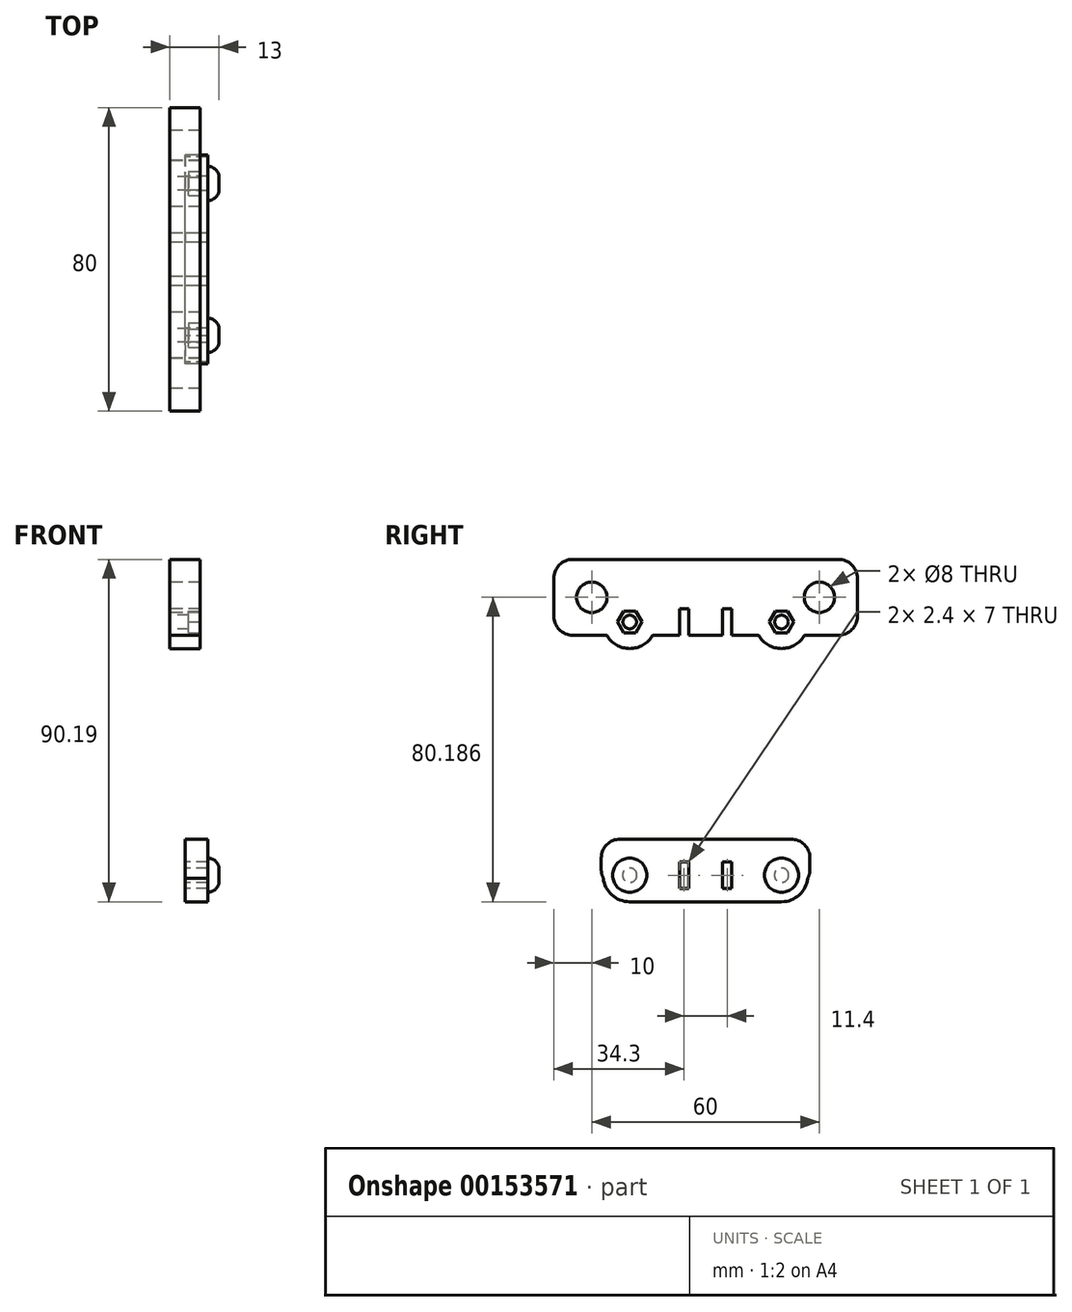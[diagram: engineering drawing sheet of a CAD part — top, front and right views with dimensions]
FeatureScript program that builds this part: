
annotation { "Feature Type Name" : "Feature", "Feature Type Description" : "" }
export const myFeature = defineFeature(function(context is Context, id is Id, definition is map)
    precondition{}
    {
        {
            var Q0;
            Q0=qCreatedBy(makeId("Right.planeOp"),FACE);
            var sketch = newSketch(context, id + "F0", { "sketchPlane" : qUnion([Q0])});
            skLineSegment(sketch, "E0", {"start": v(0, 142.5) * mm, "end": v(0, -139.74) * mm, "construction": true});
            skLineSegment(sketch, "E1.bottom", {"start": v(-35, 25) * mm, "end": v(35, 25) * mm});
            skLineSegment(sketch, "E1.top", {"start": v(-40, -25) * mm, "end": v(40, -25) * mm});
            skLineSegment(sketch, "E1.left", {"start": v(-40, 20) * mm, "end": v(-40, -25) * mm});
            skLineSegment(sketch, "E1.right", {"start": v(40, 20) * mm, "end": v(40, -25) * mm});
            skPoint(sketch, "E1.middle", {"position": v(0, 0) * mm});
            skCircle(sketch, "E2", {"center": v(-30, 13) * mm, "radius": 4 * mm});
            skCircle(sketch, "E3", {"center": v(30, 13) * mm, "radius": 4 * mm});
            skCircle(sketch, "E4", {"center": v(-30, -13) * mm, "radius": 5 * mm});
            skCircle(sketch, "E5", {"center": v(30, -13) * mm, "radius": 5 * mm});
            skPoint(sketch, "E6.visualSharp", {"position": v(-40, 25) * mm});
            skArc(sketch, "E6.filletArc", {"start": v(-35, 25) * mm, "mid": v(-38.54, 23.54) * mm, "end": v(-40, 20) * mm});
            skPoint(sketch, "E7.visualSharp", {"position": v(40, 25) * mm});
            skArc(sketch, "E7.filletArc", {"start": v(40, 20) * mm, "mid": v(38.54, 23.54) * mm, "end": v(35, 25) * mm});
            skLineSegment(sketch, "E8.bottom", {"start": v(-11, 25) * mm, "end": v(11, 25) * mm});
            skLineSegment(sketch, "E8.top", {"start": v(-9, 8) * mm, "end": v(9, 8) * mm});
            skLineSegment(sketch, "E8.left", {"start": v(-11, 25) * mm, "end": v(-11, 10) * mm});
            skLineSegment(sketch, "E8.right", {"start": v(11, 25) * mm, "end": v(11, 10) * mm});
            skPoint(sketch, "E8.middle", {"position": v(0, 16.5) * mm});
            skPoint(sketch, "E9.visualSharp", {"position": v(11, 8) * mm});
            skArc(sketch, "E9.filletArc", {"start": v(9, 8) * mm, "mid": v(10.41, 8.59) * mm, "end": v(11, 10) * mm});
            skPoint(sketch, "E10.visualSharp", {"position": v(-11, 8) * mm});
            skArc(sketch, "E10.filletArc", {"start": v(-11, 10) * mm, "mid": v(-10.41, 8.59) * mm, "end": v(-9, 8) * mm});
            skSolve(sketch);
        }
        {
            var Q0;
            Q0=makeQuery(id+"F0.imprint","IMPRINT",FACE,{"disambiguationData":[TD([[makeQuery(id+"F0.imprint","IMPRINT",EDGE,{"derivedFrom":sQuery(id+"F0.wireOp",EDGE,"E1.bottom")}),-1.0]])]});
            extrude(context, id + "F1", {"entities" : qUnion([Q0]), "depth" : 8 * mm, "symmetric" : true});
        }
        {
            var Q0;
            {var subQ0=sQuery(id+"F0.wireOp",EDGE,"E1.bottom");Q0=makeQuery(id+"F1.opExtrude","SWEPT_FACE",FACE,{"disambiguationData":[OSD([subQ0]),TDD([makeQuery(id+"F0.imprint","IMPRINT",EDGE,{"disambiguationData":[TD([[makeQuery(id+"F0.imprint","INTERSECT",VERTEX,{"derivedFrom":[subQ0,sQuery(id+"F0.wireOp",EDGE,"E7.filletArc")]}),1.0]])],"derivedFrom":subQ0})])]});}
            var sketch = newSketch(context, id + "F2", { "sketchPlane" : qUnion([Q0])});
            skCircle(sketch, "E11", {"center": v(0, 30) * mm, "radius": 1.4 * mm});
            skCircle(sketch, "E12", {"center": v(0, 24) * mm, "radius": 1.4 * mm});
            skCircle(sketch, "E13", {"center": v(0, -24) * mm, "radius": 1.4 * mm});
            skCircle(sketch, "E14", {"center": v(0, -30) * mm, "radius": 1.4 * mm});
            skLineSegment(sketch, "E15", {"start": v(-76.86, 0) * mm, "end": v(82.98, 0) * mm, "construction": true});
            skSolve(sketch);
        }
        {
            var Q0;
            Q0=qSketchRegion(id+"F2",true);
            extrude(context, id + "F3", {"entities" : qUnion([Q0]), "operationType" : NewBodyOperationType.REMOVE, "oppositeDirection" : true, "depth" : 13 * mm});
        }
        {
            var Q0;
            Q0=qCreatedBy(makeId("Right.planeOp"),FACE);
            var sketch = newSketch(context, id + "F4", { "sketchPlane" : qUnion([Q0])});
            skLineSegment(sketch, "E16", {"start": v(0, 90) * mm, "end": v(0, 27.03) * mm, "construction": true});
            skCircle(sketch, "E17", {"center": v(-30, 70.19) * mm, "radius": 4 * mm});
            skCircle(sketch, "E18", {"center": v(30, 70.19) * mm, "radius": 4 * mm});
            skLineSegment(sketch, "E19.bottom", {"start": v(-35, 80.19) * mm, "end": v(35, 80.19) * mm});
            skLineSegment(sketch, "E19.top", {"start": v(-35, 60.19) * mm, "end": v(-26.06, 60.19) * mm});
            skLineSegment(sketch, "E19.left", {"start": v(-40, 75.19) * mm, "end": v(-40, 65.19) * mm});
            skLineSegment(sketch, "E19.right", {"start": v(40, 75.19) * mm, "end": v(40, 65.19) * mm});
            skPoint(sketch, "E19.middle", {"position": v(0, 70.19) * mm});
            skPoint(sketch, "E20.visualSharp", {"position": v(-40, 80.19) * mm});
            skArc(sketch, "E20.filletArc", {"start": v(-35, 80.19) * mm, "mid": v(-38.54, 78.72) * mm, "end": v(-40, 75.19) * mm});
            skPoint(sketch, "E21.visualSharp", {"position": v(-40, 60.19) * mm});
            skArc(sketch, "E21.filletArc", {"start": v(-40, 65.19) * mm, "mid": v(-38.54, 61.65) * mm, "end": v(-35, 60.19) * mm});
            skPoint(sketch, "E22.visualSharp", {"position": v(40, 80.19) * mm});
            skArc(sketch, "E22.filletArc", {"start": v(40, 75.19) * mm, "mid": v(38.54, 78.72) * mm, "end": v(35, 80.19) * mm});
            skPoint(sketch, "E23.visualSharp", {"position": v(40, 60.19) * mm});
            skArc(sketch, "E23.filletArc", {"start": v(35, 60.19) * mm, "mid": v(38.54, 61.65) * mm, "end": v(40, 65.19) * mm});
            skLineSegment(sketch, "E24.bottom", {"start": v(-11, 80.19) * mm, "end": v(11, 80.19) * mm});
            skPoint(sketch, "E24.middle", {"position": v(0, 76.69) * mm});
            skLineSegment(sketch, "E25", {"start": v(-87.97, 70.19) * mm, "end": v(-87.97, 70.19) * mm});
            skPoint(sketch, "E25.endSnap0", {"position": v(40, 70.19) * mm});
            skLineSegment(sketch, "E26.bottom", {"start": v(-6.9, 67.19) * mm, "end": v(-4.5, 67.19) * mm});
            skLineSegment(sketch, "E26.top", {"start": v(-6.9, 60.19) * mm, "end": v(-4.5, 60.19) * mm});
            skLineSegment(sketch, "E26.left", {"start": v(-6.9, 67.19) * mm, "end": v(-6.9, 60.19) * mm});
            skLineSegment(sketch, "E26.right", {"start": v(-4.5, 67.19) * mm, "end": v(-4.5, 60.19) * mm});
            skLineSegment(sketch, "E27.bottom", {"start": v(4.5, 67.19) * mm, "end": v(6.9, 67.19) * mm});
            skLineSegment(sketch, "E27.top", {"start": v(4.5, 60.19) * mm, "end": v(6.9, 60.19) * mm});
            skLineSegment(sketch, "E27.left", {"start": v(4.5, 67.19) * mm, "end": v(4.5, 60.19) * mm});
            skLineSegment(sketch, "E27.right", {"start": v(6.9, 67.19) * mm, "end": v(6.9, 60.19) * mm});
            skCircle(sketch, "E28", {"center": v(-20, 63.69) * mm, "radius": 1.8 * mm});
            skCircle(sketch, "E29", {"center": v(20, 63.69) * mm, "radius": 1.8 * mm});
            skArc(sketch, "E30", {"start": v(-26.06, 60.19) * mm, "mid": v(-20, 56.69) * mm, "end": v(-13.94, 60.19) * mm});
            skArc(sketch, "E31.MirrorC", {"start": v(26.06, 60.19) * mm, "mid": v(20, 56.69) * mm, "end": v(13.94, 60.19) * mm});
            skLineSegment(sketch, "E32.trimOffspring", {"start": v(-13.94, 60.19) * mm, "end": v(13.94, 60.19) * mm});
            skLineSegment(sketch, "E33.trimOffspring", {"start": v(26.06, 60.19) * mm, "end": v(35, 60.19) * mm});
            skSolve(sketch);
        }
        {
            var Q0;
            Q0=makeQuery(id+"F4.imprint","IMPRINT",FACE,{"disambiguationData":[TD([[makeQuery(id+"F4.imprint","IMPRINT",EDGE,{"derivedFrom":sQuery(id+"F4.wireOp",EDGE,"E17")}),-1.0]])]});
            extrude(context, id + "F5", {"entities" : qUnion([Q0]), "depth" : 8 * mm, "symmetric" : true});
        }
        {
            var Q0;
            Q0=makeQuery(id+"F5.opExtrude","CAP_FACE",FACE,{"disambiguationData":[OSD([sQuery(id+"F4.wireOp",EDGE,"E17"),sQuery(id+"F4.wireOp",EDGE,"E18"),sQuery(id+"F4.wireOp",EDGE,"E19.bottom"),sQuery(id+"F4.wireOp",EDGE,"E19.top"),sQuery(id+"F4.wireOp",EDGE,"E19.left"),sQuery(id+"F4.wireOp",EDGE,"E19.right"),sQuery(id+"F4.wireOp",EDGE,"E20.filletArc"),sQuery(id+"F4.wireOp",EDGE,"E21.filletArc"),sQuery(id+"F4.wireOp",EDGE,"E22.filletArc"),sQuery(id+"F4.wireOp",EDGE,"E23.filletArc"),sQuery(id+"F4.wireOp",EDGE,"E24.bottom"),sQuery(id+"F4.wireOp",EDGE,"E26.bottom"),sQuery(id+"F4.wireOp",EDGE,"E26.left"),sQuery(id+"F4.wireOp",EDGE,"E26.right"),sQuery(id+"F4.wireOp",EDGE,"E27.bottom"),sQuery(id+"F4.wireOp",EDGE,"E27.left"),sQuery(id+"F4.wireOp",EDGE,"E27.right"),sQuery(id+"F4.wireOp",EDGE,"E28"),sQuery(id+"F4.wireOp",EDGE,"E29")])],"isStart":false});
            var sketch = newSketch(context, id + "F6", { "sketchPlane" : qUnion([Q0])});
            skCircle(sketch, "E34.cCircle", {"center": v(20, 63.69) * mm, "radius": 2.8 * mm, "construction": true});
            skLineSegment(sketch, "E34.0", {"start": v(18.38, 66.49) * mm, "end": v(21.62, 66.49) * mm});
            skLineSegment(sketch, "E34.1", {"start": v(21.62, 66.49) * mm, "end": v(23.23, 63.69) * mm});
            skLineSegment(sketch, "E34.2", {"start": v(23.23, 63.69) * mm, "end": v(21.62, 60.89) * mm});
            skLineSegment(sketch, "E34.3", {"start": v(21.62, 60.89) * mm, "end": v(18.38, 60.89) * mm});
            skLineSegment(sketch, "E34.4", {"start": v(18.38, 60.89) * mm, "end": v(16.77, 63.69) * mm});
            skLineSegment(sketch, "E34.5", {"start": v(16.77, 63.69) * mm, "end": v(18.38, 66.49) * mm});
            skPoint(sketch, "E34.0.midPoint", {"position": v(20, 66.49) * mm});
            skCircle(sketch, "E35.cCircle", {"center": v(-20, 63.69) * mm, "radius": 2.8 * mm, "construction": true});
            skLineSegment(sketch, "E35.0", {"start": v(-21.62, 66.49) * mm, "end": v(-18.38, 66.49) * mm});
            skLineSegment(sketch, "E35.1", {"start": v(-18.38, 66.49) * mm, "end": v(-16.77, 63.69) * mm});
            skLineSegment(sketch, "E35.2", {"start": v(-16.77, 63.69) * mm, "end": v(-18.38, 60.89) * mm});
            skLineSegment(sketch, "E35.3", {"start": v(-18.38, 60.89) * mm, "end": v(-21.62, 60.89) * mm});
            skLineSegment(sketch, "E35.4", {"start": v(-21.62, 60.89) * mm, "end": v(-23.23, 63.69) * mm});
            skLineSegment(sketch, "E35.5", {"start": v(-23.23, 63.69) * mm, "end": v(-21.62, 66.49) * mm});
            skPoint(sketch, "E35.0.midPoint", {"position": v(-20, 66.49) * mm});
            skSolve(sketch);
        }
        {
            var Q0;
            Q0=qSketchRegion(id+"F6",true);
            extrude(context, id + "F7", {"entities" : qUnion([Q0]), "operationType" : NewBodyOperationType.REMOVE, "oppositeDirection" : true, "depth" : 3 * mm});
        }
        {
            var Q0;
            Q0=qCreatedBy(makeId("Right.planeOp"),FACE);
            var sketch = newSketch(context, id + "F8", { "sketchPlane" : qUnion([Q0])});
            skLineSegment(sketch, "E36.bottom", {"start": v(-22.5, 6.5) * mm, "end": v(22.5, 6.5) * mm});
            skLineSegment(sketch, "E36.top", {"start": v(-6.9, -6.5) * mm, "end": v(-4.5, -6.5) * mm});
            skLineSegment(sketch, "E36.left", {"start": v(-27.5, 1.5) * mm, "end": v(-27.5, -1.5) * mm});
            skLineSegment(sketch, "E36.right", {"start": v(27.5, 1.5) * mm, "end": v(27.5, -1.5) * mm});
            skPoint(sketch, "E36.middle", {"position": v(0, 0) * mm});
            skPoint(sketch, "E37.visualSharp", {"position": v(-27.5, 6.5) * mm});
            skArc(sketch, "E37.filletArc", {"start": v(-22.5, 6.5) * mm, "mid": v(-26.04, 5.04) * mm, "end": v(-27.5, 1.5) * mm});
            skPoint(sketch, "E38.visualSharp", {"position": v(-27.5, -6.5) * mm});
            skArc(sketch, "E38.filletArc", {"start": v(-27.5, -1.5) * mm, "mid": v(-27.36, -2.66) * mm, "end": v(-26.96, -3.76) * mm});
            skPoint(sketch, "E39.visualSharp", {"position": v(27.5, 6.5) * mm});
            skArc(sketch, "E39.filletArc", {"start": v(27.5, 1.5) * mm, "mid": v(26.04, 5.04) * mm, "end": v(22.5, 6.5) * mm});
            skPoint(sketch, "E40.visualSharp", {"position": v(27.5, -6.5) * mm});
            skArc(sketch, "E40.filletArc", {"start": v(26.96, -3.76) * mm, "mid": v(27.36, -2.66) * mm, "end": v(27.5, -1.5) * mm});
            skLineSegment(sketch, "E41.bottom", {"start": v(-6.9, 0.5) * mm, "end": v(-4.5, 0.5) * mm});
            skLineSegment(sketch, "E41.left", {"start": v(-6.9, 0.5) * mm, "end": v(-6.9, -6.5) * mm});
            skLineSegment(sketch, "E41.right", {"start": v(-4.5, 0.5) * mm, "end": v(-4.5, -6.5) * mm});
            skLineSegment(sketch, "E42.MirrorCS", {"start": v(6.9, 0.5) * mm, "end": v(4.5, 0.5) * mm});
            skLineSegment(sketch, "E43.MirrorCS", {"start": v(6.9, -6.5) * mm, "end": v(4.5, -6.5) * mm});
            skLineSegment(sketch, "E44.MirrorCS", {"start": v(4.5, 0.5) * mm, "end": v(4.5, -6.5) * mm});
            skLineSegment(sketch, "E45.MirrorCS", {"start": v(6.9, 0.5) * mm, "end": v(6.9, -6.5) * mm});
            skCircle(sketch, "E46", {"center": v(20, -3) * mm, "radius": 1.9 * mm});
            skCircle(sketch, "E47.MirrorC", {"center": v(-20, -3) * mm, "radius": 1.9 * mm});
            skArc(sketch, "E48", {"start": v(-26.96, -3.76) * mm, "mid": v(-24.64, -8.24) * mm, "end": v(-19.91, -10) * mm});
            skArc(sketch, "E49.MirrorC", {"start": v(26.96, -3.76) * mm, "mid": v(24.67, -8.21) * mm, "end": v(20, -10) * mm});
            skPoint(sketch, "E50.orphan", {"position": v(22.5, -6.5) * mm});
            skLineSegment(sketch, "E51", {"start": v(-20.09, -10) * mm, "end": v(20, -10) * mm});
            skLineSegment(sketch, "E52.trimOffspring", {"start": v(4.5, -6.5) * mm, "end": v(6.9, -6.5) * mm});
            skSolve(sketch);
        }
        {
            var Q0;
            Q0=makeQuery(id+"F8.imprint","IMPRINT",FACE,{"disambiguationData":[TD([[makeQuery(id+"F8.imprint","IMPRINT",EDGE,{"derivedFrom":sQuery(id+"F8.wireOp",EDGE,"E36.bottom")}),-1.0]])]});
            extrude(context, id + "F9", {"entities" : qUnion([Q0]), "depth" : 6 * mm});
        }
        {
            var Q0;
            Q0=makeQuery(id+"F1.opExtrude","SWEPT_BODY",BODY,{"disambiguationData":[OSD([sQuery(id+"F0.wireOp",EDGE,"E1.bottom"),sQuery(id+"F0.wireOp",EDGE,"E1.top"),sQuery(id+"F0.wireOp",EDGE,"E1.left"),sQuery(id+"F0.wireOp",EDGE,"E1.right"),sQuery(id+"F0.wireOp",EDGE,"E2"),sQuery(id+"F0.wireOp",EDGE,"E3"),sQuery(id+"F0.wireOp",EDGE,"E4"),sQuery(id+"F0.wireOp",EDGE,"E5"),sQuery(id+"F0.wireOp",EDGE,"E6.filletArc"),sQuery(id+"F0.wireOp",EDGE,"E7.filletArc"),sQuery(id+"F0.wireOp",EDGE,"E8.top"),sQuery(id+"F0.wireOp",EDGE,"E8.left"),sQuery(id+"F0.wireOp",EDGE,"E8.right"),sQuery(id+"F0.wireOp",EDGE,"E9.filletArc"),sQuery(id+"F0.wireOp",EDGE,"E10.filletArc")])]});
            deleteBodies(context, id + "F10", {"entities" : qUnion([Q0])});
        }
        {
            var Q0;
            Q0=makeQuery(id+"F9.opExtrude","CAP_FACE",FACE,{"disambiguationData":[OSD([sQuery(id+"F8.wireOp",EDGE,"E36.bottom"),sQuery(id+"F8.wireOp",EDGE,"E36.top"),sQuery(id+"F8.wireOp",EDGE,"E36.left"),sQuery(id+"F8.wireOp",EDGE,"E36.right"),sQuery(id+"F8.wireOp",EDGE,"E37.filletArc"),sQuery(id+"F8.wireOp",EDGE,"E38.filletArc"),sQuery(id+"F8.wireOp",EDGE,"E39.filletArc"),sQuery(id+"F8.wireOp",EDGE,"E40.filletArc"),sQuery(id+"F8.wireOp",EDGE,"E41.bottom"),sQuery(id+"F8.wireOp",EDGE,"E41.left"),sQuery(id+"F8.wireOp",EDGE,"E41.right"),sQuery(id+"F8.wireOp",EDGE,"E42.MirrorCS"),sQuery(id+"F8.wireOp",EDGE,"E44.MirrorCS"),sQuery(id+"F8.wireOp",EDGE,"E45.MirrorCS"),sQuery(id+"F8.wireOp",EDGE,"E46"),sQuery(id+"F8.wireOp",EDGE,"E47.MirrorC")])],"isStart":false});
            var sketch = newSketch(context, id + "F11", { "sketchPlane" : qUnion([Q0])});
            skCircle(sketch, "E53", {"center": v(-20, -3) * mm, "radius": 4.5 * mm});
            skCircle(sketch, "E54.MirrorC", {"center": v(20, -3) * mm, "radius": 4.5 * mm});
            skSolve(sketch);
        }
        {
            var Q0;
            Q0=qSketchRegion(id+"F11",true);
            extrude(context, id + "F12", {"entities" : qUnion([Q0]), "operationType" : NewBodyOperationType.ADD, "depth" : 3 * mm});
        }
        {
            var Q0;
            Q0=makeQuery(id+"F12.opExtrude","CAP_EDGE",EDGE,{"disambiguationData":[OSD([sQuery(id+"F11.wireOp",EDGE,"E53")])],"isStart":false});
            var Q1;
            Q1=makeQuery(id+"F12.opExtrude","CAP_EDGE",EDGE,{"disambiguationData":[OSD([sQuery(id+"F11.wireOp",EDGE,"E54.MirrorC")])],"isStart":false});
            fillet(context, id + "F13", {"entities" : qUnion([Q0, Q1]), "radius" : 3 * mm, "tangentPropagation" : true, "allowEdgeOverflow" : false});
        }
    });
